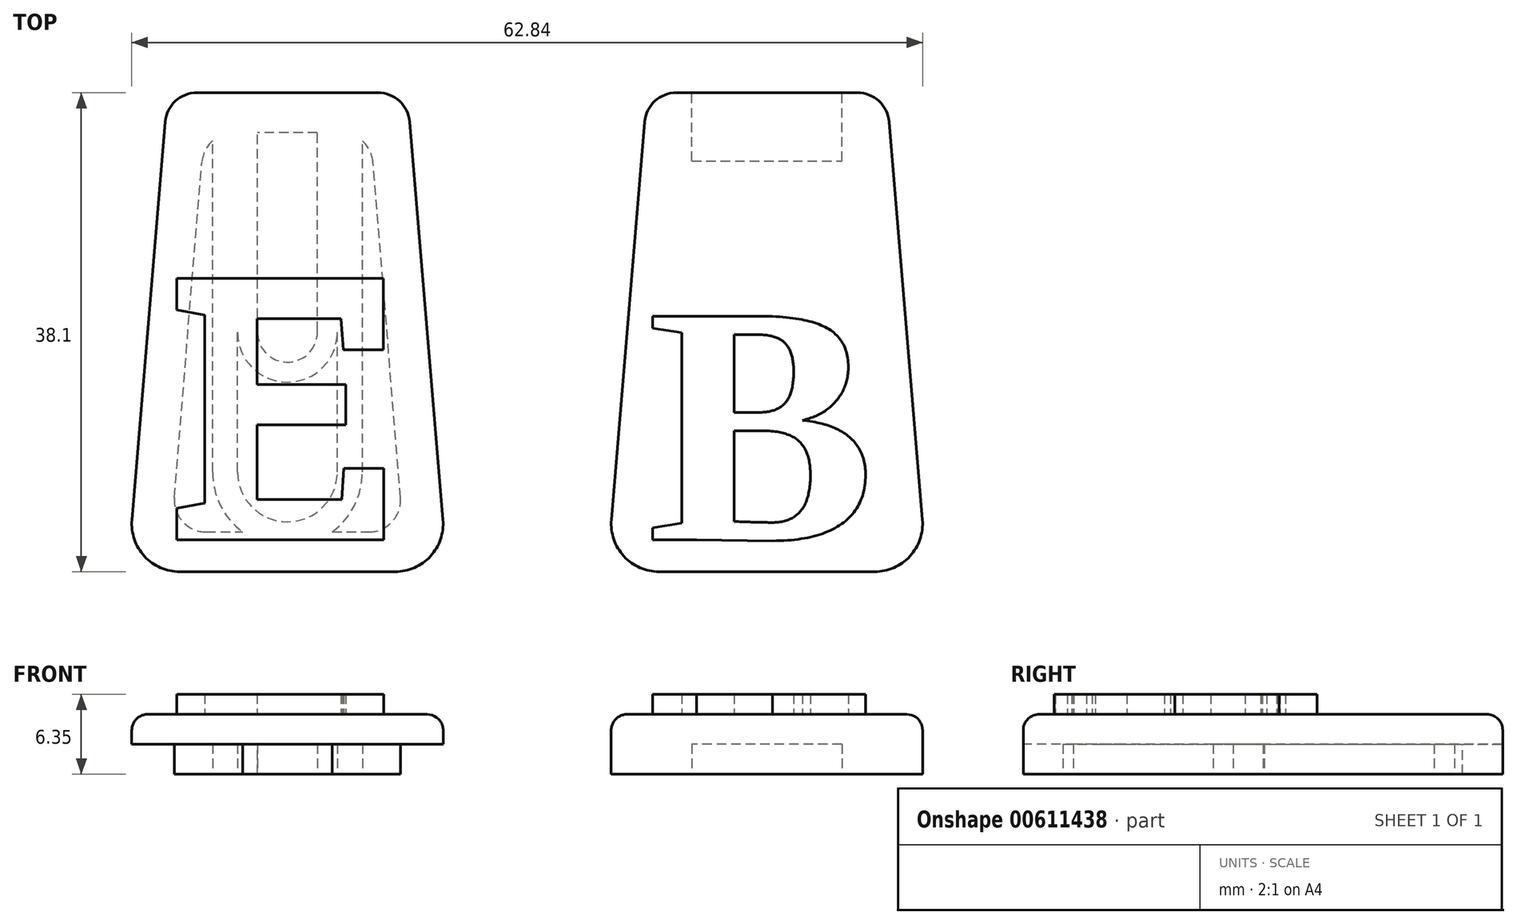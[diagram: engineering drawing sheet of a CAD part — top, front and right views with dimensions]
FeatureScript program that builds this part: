
annotation { "Feature Type Name" : "Feature", "Feature Type Description" : "" }
export const myFeature = defineFeature(function(context is Context, id is Id, definition is map)
    precondition{}
    {
        {
            var Q0;
            Q0=qCreatedBy(makeId("Top.planeOp"),FACE);
            var sketch = newSketch(context, id + "F0", { "sketchPlane" : qUnion([Q0])});
            skLineSegment(sketch, "E0", {"start": v(0, 70.74) * mm, "end": v(0, -75) * mm, "construction": true});
            skLineSegment(sketch, "E1", {"start": v(0, 30.16) * mm, "end": v(-7.19, 30.16) * mm});
            skLineSegment(sketch, "E2", {"start": v(-9.72, 27.83) * mm, "end": v(-12.36, -3.81) * mm});
            skLineSegment(sketch, "E3", {"start": v(-8.56, -7.94) * mm, "end": v(0, -7.94) * mm});
            skPoint(sketch, "E4.visualSharp", {"position": v(-9.52, 30.16) * mm});
            skArc(sketch, "E4.filletArc", {"start": v(-7.19, 30.16) * mm, "mid": v(-8.9, 29.5) * mm, "end": v(-9.72, 27.83) * mm});
            skPoint(sketch, "E5.visualSharp", {"position": v(-12.7, -7.94) * mm});
            skArc(sketch, "E5.filletArc", {"start": v(-12.36, -3.81) * mm, "mid": v(-11.36, -6.7) * mm, "end": v(-8.56, -7.94) * mm});
            skArc(sketch, "E6.MirrorCS", {"start": v(7.19, 30.16) * mm, "mid": v(8.9, 29.5) * mm, "end": v(9.72, 27.83) * mm});
            skPoint(sketch, "E7.MirrorP", {"position": v(12.7, -7.94) * mm});
            skPoint(sketch, "E8.MirrorP", {"position": v(9.52, 30.16) * mm});
            skArc(sketch, "E9.MirrorCS", {"start": v(12.36, -3.81) * mm, "mid": v(11.36, -6.7) * mm, "end": v(8.56, -7.94) * mm});
            skLineSegment(sketch, "E10.MirrorCS", {"start": v(8.56, -7.94) * mm, "end": v(0, -7.94) * mm});
            skLineSegment(sketch, "E11.MirrorCS", {"start": v(0, 30.16) * mm, "end": v(7.19, 30.16) * mm});
            skLineSegment(sketch, "E12.MirrorCS", {"start": v(9.72, 27.83) * mm, "end": v(12.36, -3.81) * mm});
            skLineSegment(sketch, "E13", {"start": v(19.05, 69.77) * mm, "end": v(19.05, -54.28) * mm, "construction": true});
            skArc(sketch, "E14.MirrorCS", {"start": v(30.91, 30.16) * mm, "mid": v(29.2, 29.5) * mm, "end": v(28.38, 27.83) * mm});
            skArc(sketch, "E15.MirrorCS", {"start": v(45.29, 30.16) * mm, "mid": v(47, 29.5) * mm, "end": v(47.82, 27.83) * mm});
            skPoint(sketch, "E16.MirrorP", {"position": v(28.58, 30.16) * mm});
            skPoint(sketch, "E17.MirrorP", {"position": v(50.8, -7.94) * mm});
            skLineSegment(sketch, "E18.MirrorCS", {"start": v(46.66, -7.94) * mm, "end": v(38.1, -7.94) * mm});
            skLineSegment(sketch, "E19.MirrorCS", {"start": v(38.1, 30.16) * mm, "end": v(45.29, 30.16) * mm});
            skArc(sketch, "E20.MirrorCS", {"start": v(25.74, -3.81) * mm, "mid": v(26.74, -6.7) * mm, "end": v(29.54, -7.94) * mm});
            skArc(sketch, "E21.MirrorCS", {"start": v(50.46, -3.81) * mm, "mid": v(49.46, -6.7) * mm, "end": v(46.66, -7.94) * mm});
            skLineSegment(sketch, "E22.MirrorCS", {"start": v(28.38, 27.83) * mm, "end": v(25.74, -3.81) * mm});
            skLineSegment(sketch, "E23.MirrorCS", {"start": v(38.1, 30.16) * mm, "end": v(30.91, 30.16) * mm});
            skLineSegment(sketch, "E24.MirrorCS", {"start": v(29.54, -7.94) * mm, "end": v(38.1, -7.94) * mm});
            skLineSegment(sketch, "E25.MirrorCS", {"start": v(47.82, 27.83) * mm, "end": v(50.46, -3.81) * mm});
            skPoint(sketch, "E26.MirrorP", {"position": v(25.4, -7.94) * mm});
            skPoint(sketch, "E27.MirrorP", {"position": v(47.63, 30.16) * mm});
            skSolve(sketch);
        }
        {
            var Q0;
            Q0 = qSketchRegion(id + "F0", true);
            extrude(context, id + "F1", {"entities" : qUnion([Q0]), "depth" : 4.76 * mm, "offsetDistance" : 25.4 * mm});
        }
        {
            var Q0;
            Q0=makeQuery(id+"F1.opExtrude","CAP_FACE",FACE,{"disambiguationData":[OSD([sQuery(id+"F0.wireOp",EDGE,"E1"),sQuery(id+"F0.wireOp",EDGE,"E2"),sQuery(id+"F0.wireOp",EDGE,"E3"),sQuery(id+"F0.wireOp",EDGE,"E4.filletArc"),sQuery(id+"F0.wireOp",EDGE,"E5.filletArc"),sQuery(id+"F0.wireOp",EDGE,"E6.MirrorCS"),sQuery(id+"F0.wireOp",EDGE,"E9.MirrorCS"),sQuery(id+"F0.wireOp",EDGE,"E10.MirrorCS"),sQuery(id+"F0.wireOp",EDGE,"E11.MirrorCS"),sQuery(id+"F0.wireOp",EDGE,"E12.MirrorCS")])],"isStart":false});
            var sketch = newSketch(context, id + "F2", { "sketchPlane" : qUnion([Q0])});
            skText(sketch, "E28", { "text": "E", "fontName": "RobotoSlab-Bold.ttf"});
            skText(sketch, "E29", { "text": "B", "fontName": "Tinos-Bold.ttf"});
            const initialGuessF2  = {"E28": [-0.0096, -0.0054, 1, 0, 0.02107], "E29": [0.02858, -0.0054, 1, 0, 0.01955]};
            skSetInitialGuess(sketch, initialGuessF2);
            skSolve(sketch);
        }
        {
            var Q0;
            Q0=makeQuery(id+"F1.opExtrude","CAP_EDGE",EDGE,{"disambiguationData":[OSD([sQuery(id+"F0.wireOp",EDGE,"E2")])],"isStart":false});
            var Q1;
            Q1=makeQuery(id+"F1.opExtrude","CAP_EDGE",EDGE,{"disambiguationData":[OSD([sQuery(id+"F0.wireOp",EDGE,"E22.MirrorCS")])],"isStart":false});
            fillet(context, id + "F3", {"entities" : qUnion([Q0, Q1]), "radius" : 1.27 * mm, "tangentPropagation" : true, "allowEdgeOverflow" : false});
        }
        {
            var Q0;
            Q0 = qSketchRegion(id + "F2", true);
            extrude(context, id + "F4", {"entities" : qUnion([Q0]), "operationType" : NewBodyOperationType.ADD, "depth" : 1.59 * mm, "offsetDistance" : 25.4 * mm});
        }
        {
            var Q0;
            Q0=qCreatedBy(makeId("Top.planeOp"),FACE);
            var sketch = newSketch(context, id + "F5", { "sketchPlane" : qUnion([Q0])});
            skArc(sketch, "E30", {"start": v(-3.97, 0) * mm, "mid": v(0, -3.97) * mm, "end": v(3.97, 0) * mm});
            skArc(sketch, "E31", {"start": v(-5.95, 0) * mm, "mid": v(0, -5.95) * mm, "end": v(5.95, 0) * mm});
            skLineSegment(sketch, "E32", {"start": v(-5.95, 0) * mm, "end": v(-5.95, 35.47) * mm});
            skLineSegment(sketch, "E33", {"start": v(-5.95, 35.47) * mm, "end": v(-2.38, 35.47) * mm});
            skLineSegment(sketch, "E34", {"start": v(5.95, 0) * mm, "end": v(5.95, 35.47) * mm});
            skLineSegment(sketch, "E35", {"start": v(-3.97, 0) * mm, "end": v(-3.97, 11.11) * mm});
            skLineSegment(sketch, "E36", {"start": v(3.97, 0) * mm, "end": v(3.97, 11.11) * mm});
            skPoint(sketch, "E37", {"position": v(0, 11.11) * mm});
            skArc(sketch, "E38", {"start": v(-3.97, 11.11) * mm, "mid": v(0, 7.14) * mm, "end": v(3.97, 11.11) * mm});
            skArc(sketch, "E39", {"start": v(-2.38, 11.13) * mm, "mid": v(0.05, 8.73) * mm, "end": v(2.38, 11.22) * mm});
            skLineSegment(sketch, "E40", {"start": v(-2.38, 11.1) * mm, "end": v(-2.38, 35.47) * mm});
            skLineSegment(sketch, "E41", {"start": v(2.38, 11.22) * mm, "end": v(2.38, 35.47) * mm});
            skLineSegment(sketch, "E42.trimOffspring", {"start": v(2.38, 35.47) * mm, "end": v(5.95, 35.47) * mm});
            skSolve(sketch);
        }
        {
            var Q0;
            Q0=makeQuery(id+"F5.imprint","IMPRINT",FACE,{"disambiguationData":[TD([[makeQuery(id+"F5.imprint","IMPRINT",EDGE,{"derivedFrom":sQuery(id+"F5.wireOp",EDGE,"E30")}),-1.0]])]});
            extrude(context, id + "F6", {"entities" : qUnion([Q0]), "operationType" : NewBodyOperationType.REMOVE, "depth" : 2.38 * mm, "offsetDistance" : 25.4 * mm});
        }
        {
            var Q0;
            Q0=qCreatedBy(makeId("Top.planeOp"),FACE);
            var sketch = newSketch(context, id + "F7", { "sketchPlane" : qUnion([Q0])});
            skLineSegment(sketch, "E43", {"start": v(0, -12.96) * mm, "end": v(0, 33.33) * mm, "construction": true});
            skLineSegment(sketch, "E44", {"start": v(-15.3, -7.95) * mm, "end": v(66.65, -7.95) * mm, "construction": true});
            skLineSegment(sketch, "E45", {"start": v(-14.69, 30.15) * mm, "end": v(65.21, 30.15) * mm, "construction": true});
            skLineSegment(sketch, "E46", {"start": v(38.1, -15.72) * mm, "end": v(38.1, 44.25) * mm, "construction": true});
            skLineSegment(sketch, "E47", {"start": v(19.05, -21.33) * mm, "end": v(19.05, 44.77) * mm, "construction": true});
            skLineSegment(sketch, "E48", {"start": v(0, 26.97) * mm, "end": v(-4.27, 26.97) * mm});
            skLineSegment(sketch, "E49", {"start": v(-12.28, -3.3) * mm, "end": v(-9.86, 26.16) * mm, "construction": true});
            skLineSegment(sketch, "E50", {"start": v(0, -4.78) * mm, "end": v(-6.46, -4.78) * mm});
            skLineSegment(sketch, "E51", {"start": v(-8.99, -2.03) * mm, "end": v(-6.8, 24.64) * mm});
            skPoint(sketch, "E52.visualSharp", {"position": v(-9.21, -4.78) * mm});
            skArc(sketch, "E52.filletArc", {"start": v(-8.99, -2.03) * mm, "mid": v(-8.32, -3.96) * mm, "end": v(-6.46, -4.78) * mm});
            skPoint(sketch, "E53.visualSharp", {"position": v(-6.6, 26.97) * mm});
            skArc(sketch, "E53.filletArc", {"start": v(-4.27, 26.97) * mm, "mid": v(-5.99, 26.3) * mm, "end": v(-6.8, 24.64) * mm});
            skPoint(sketch, "E54.MirrorP", {"position": v(9.21, -4.78) * mm});
            skLineSegment(sketch, "E55.MirrorCS", {"start": v(0, 26.97) * mm, "end": v(4.27, 26.97) * mm});
            skArc(sketch, "E56.MirrorCS", {"start": v(8.99, -2.03) * mm, "mid": v(8.32, -3.96) * mm, "end": v(6.46, -4.78) * mm});
            skPoint(sketch, "E57.MirrorP", {"position": v(6.6, 26.97) * mm});
            skLineSegment(sketch, "E58.MirrorCS", {"start": v(12.28, -3.3) * mm, "end": v(9.86, 26.16) * mm, "construction": true});
            skLineSegment(sketch, "E59.MirrorCS", {"start": v(0, -4.78) * mm, "end": v(6.46, -4.78) * mm});
            skLineSegment(sketch, "E60.MirrorCS", {"start": v(8.99, -2.03) * mm, "end": v(6.8, 24.64) * mm});
            skArc(sketch, "E61.MirrorCS", {"start": v(4.27, 26.97) * mm, "mid": v(5.99, 26.3) * mm, "end": v(6.8, 24.64) * mm});
            skLineSegment(sketch, "E62.bottom", {"start": v(-16.67, -10.95) * mm, "end": v(14.75, -10.95) * mm});
            skLineSegment(sketch, "E62.top", {"start": v(-16.67, 32.62) * mm, "end": v(14.75, 32.62) * mm});
            skLineSegment(sketch, "E62.left", {"start": v(-16.67, -10.95) * mm, "end": v(-16.67, 32.62) * mm});
            skLineSegment(sketch, "E62.right", {"start": v(14.75, -10.95) * mm, "end": v(14.75, 32.62) * mm});
            skArc(sketch, "E63.0", {"start": v(48.35, -1.92) * mm, "mid": v(47.36, -4.82) * mm, "end": v(44.56, -6.05) * mm});
            skLineSegment(sketch, "E63.1", {"start": v(38.1, -6.05) * mm, "end": v(44.56, -6.05) * mm});
            skLineSegment(sketch, "E63.2", {"start": v(48.35, -1.92) * mm, "end": v(46.17, 24.75) * mm});
            skLineSegment(sketch, "E63.3", {"start": v(38.1, -6.05) * mm, "end": v(31.64, -6.05) * mm});
            skArc(sketch, "E63.4", {"start": v(27.85, -1.92) * mm, "mid": v(28.84, -4.82) * mm, "end": v(31.64, -6.05) * mm});
            skLineSegment(sketch, "E63.5", {"start": v(27.85, -1.92) * mm, "end": v(30.03, 24.75) * mm});
            skArc(sketch, "E63.6", {"start": v(42.37, 28.24) * mm, "mid": v(44.95, 27.24) * mm, "end": v(46.17, 24.75) * mm});
            skLineSegment(sketch, "E63.7", {"start": v(42.3, 28.24) * mm, "end": v(42.37, 28.24) * mm});
            skArc(sketch, "E63.9", {"start": v(33.83, 28.24) * mm, "mid": v(31.25, 27.24) * mm, "end": v(30.03, 24.75) * mm});
            skPoint(sketch, "E64.MirrorCS.start.orphan", {"position": v(38.1, -4.78) * mm});
            skPoint(sketch, "E65.MirrorCS.end.orphan", {"position": v(44.56, -4.78) * mm});
            skPoint(sketch, "E66.MirrorCS.start.orphan", {"position": v(47.09, -2.03) * mm});
            skPoint(sketch, "E67.MirrorCS.end.orphan", {"position": v(31.64, -4.78) * mm});
            skPoint(sketch, "E68.MirrorCS.start.orphan", {"position": v(29.11, -2.03) * mm});
            skPoint(sketch, "E69.MirrorCS.end.orphan", {"position": v(31.3, 24.64) * mm});
            skPoint(sketch, "E70.MirrorCS.end.orphan", {"position": v(33.83, 26.97) * mm});
            skPoint(sketch, "E70.MirrorCS.start.orphan", {"position": v(38.1, 26.97) * mm});
            skPoint(sketch, "E71.MirrorCS.end.orphan", {"position": v(44.9, 24.64) * mm});
            skPoint(sketch, "E72.MirrorCS.end.orphan", {"position": v(42.37, 26.97) * mm});
            skLineSegment(sketch, "E73.top", {"start": v(33.83, 33.18) * mm, "end": v(42.3, 33.18) * mm});
            skLineSegment(sketch, "E73.left", {"start": v(33.83, 28.24) * mm, "end": v(33.83, 33.18) * mm});
            skLineSegment(sketch, "E73.right", {"start": v(42.3, 28.24) * mm, "end": v(42.3, 33.18) * mm});
            skSolve(sketch);
        }
        {
            var Q0;
            Q0=makeQuery(id+"F7.imprint","IMPRINT",FACE,{"disambiguationData":[TD([[makeQuery(id+"F7.imprint","IMPRINT",EDGE,{"derivedFrom":sQuery(id+"F7.wireOp",EDGE,"E63.0")}),-1.0]])]});
            var Q1;
            Q1=makeQuery(id+"F7.imprint","IMPRINT",FACE,{"disambiguationData":[TD([[makeQuery(id+"F7.imprint","IMPRINT",EDGE,{"derivedFrom":sQuery(id+"F7.wireOp",EDGE,"E48")}),-1.0]])]});
            extrude(context, id + "F8", {"entities" : qUnion([Q0, Q1]), "operationType" : NewBodyOperationType.REMOVE, "depth" : 2.38 * mm, "offsetDistance" : 25.4 * mm});
        }
        {
            var Q0;
            Q0=qCreatedBy(makeId("Top.planeOp"),FACE);
            var sketch = newSketch(context, id + "F9", { "sketchPlane" : qUnion([Q0])});
            skLineSegment(sketch, "E74.bottom", {"start": v(32.13, 24.73) * mm, "end": v(44.07, 24.73) * mm});
            skLineSegment(sketch, "E74.top", {"start": v(32.13, 34.6) * mm, "end": v(44.07, 34.6) * mm});
            skLineSegment(sketch, "E74.left", {"start": v(32.13, 24.73) * mm, "end": v(32.13, 34.6) * mm});
            skLineSegment(sketch, "E74.right", {"start": v(44.07, 24.73) * mm, "end": v(44.07, 34.6) * mm});
            skLineSegment(sketch, "E75", {"start": v(38.1, 4.25) * mm, "end": v(38.1, 53.12) * mm, "construction": true});
            skSolve(sketch);
        }
        {
            var Q0;
            Q0 = qSketchRegion(id + "F9", true);
            extrude(context, id + "F10", {"entities" : qUnion([Q0]), "operationType" : NewBodyOperationType.REMOVE, "depth" : 2.38 * mm, "offsetDistance" : 25.4 * mm});
        }
    });
